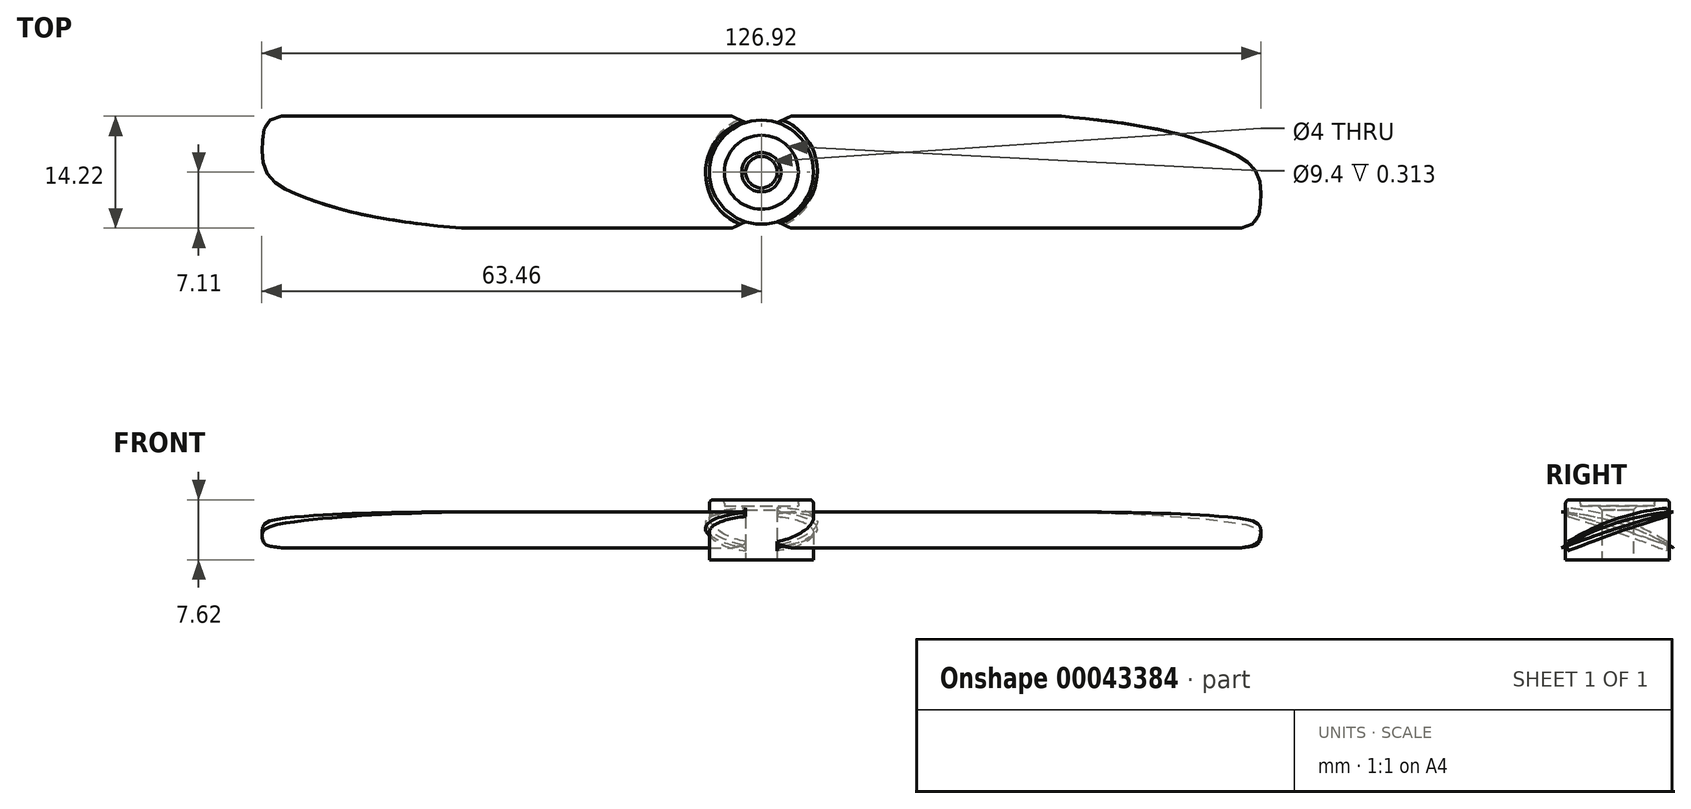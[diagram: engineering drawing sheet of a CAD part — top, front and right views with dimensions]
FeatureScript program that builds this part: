
annotation { "Feature Type Name" : "Feature", "Feature Type Description" : "" }
export const myFeature = defineFeature(function(context is Context, id is Id, definition is map)
    precondition{}
    {
        {
            var Q0;
            Q0=qCreatedBy(makeId("Front.planeOp"),FACE);
            var sketch = newSketch(context, id + "F0", { "sketchPlane" : qUnion([Q0])});
            skLineSegment(sketch, "E0", {"start": v(0, 0) * mm, "end": v(0, 9.6) * mm, "construction": true});
            skLineSegment(sketch, "E1", {"start": v(2, 0) * mm, "end": v(2, 6.8) * mm});
            skLineSegment(sketch, "E2", {"start": v(2, 6.8) * mm, "end": v(4.7, 6.8) * mm});
            skLineSegment(sketch, "E3", {"start": v(4.7, 6.8) * mm, "end": v(4.7, 7.62) * mm});
            skLineSegment(sketch, "E4", {"start": v(4.7, 7.62) * mm, "end": v(6.6, 7.62) * mm});
            skLineSegment(sketch, "E5", {"start": v(6.6, 7.62) * mm, "end": v(6.6, 0) * mm});
            skLineSegment(sketch, "E6", {"start": v(6.6, 0) * mm, "end": v(2, 0) * mm});
            skSolve(sketch);
        }
        {
            var Q0;
            Q0 = qSketchRegion(id + "F0", true);
            var Q1;
            Q1=sQuery(id+"F0.wireOp",EDGE,"E0");
            revolve(context, id + "F1", {"entities" : qUnion([Q0]), "axis" : qUnion([Q1]), "revolveType" : RevolveType.FULL});
        }
        {
            var Q0;
            Q0=makeQuery(id+"F1.opRevolve","SWEPT_EDGE",EDGE,{"disambiguationData":[OSD([sQuery(id+"F0.wireOp",EDGE,"E1"),sQuery(id+"F0.wireOp",EDGE,"E2")])]});
            chamfer(context, id + "F2", {"entities" : qUnion([Q0]), "width" : .5 * mm, "tangentPropagation" : true});
        }
        {
            var Q0;
            Q0=makeQuery(id+"F1.opRevolve","SWEPT_EDGE",EDGE,{"disambiguationData":[OSD([sQuery(id+"F0.wireOp",EDGE,"E4"),sQuery(id+"F0.wireOp",EDGE,"E5")])]});
            var Q1;
            Q1=makeQuery(id+"F1.opRevolve","SWEPT_EDGE",EDGE,{"disambiguationData":[OSD([sQuery(id+"F0.wireOp",EDGE,"E3"),sQuery(id+"F0.wireOp",EDGE,"E4")])]});
            fillet(context, id + "F3", {"entities" : qUnion([Q0, Q1]), "radius" : .5 * mm, "tangentPropagation" : true, "allowEdgeOverflow" : false});
        }
        {
            var Q0;
            Q0=qCreatedBy(makeId("Right.planeOp"),FACE);
            cPlane(context, id + "F4", {"entities" : qUnion([Q0]), "cplaneType" : CPlaneType.OFFSET, "offset" : 2 * mm, "width" : 152.4 * mm, "height" : 152.4 * mm});
        }
        {
            var Q0;
            Q0=qCreatedBy(id+"F4.planeOp",FACE);
            var sketch = newSketch(context, id + "F5", { "sketchPlane" : qUnion([Q0])});
            skFitSpline(sketch, "E7", {"points": [v(7.11, 6.1) * mm, v(-7.11, 1.52) * mm], "startDerivative": vector(-15.31, -1.42) * mm, "endDerivative": vector(-14.1, -8.25) * mm});
            skFitSpline(sketch, "E8", {"points": [v(7.11, 6.1) * mm, v(-7.11, 1.52) * mm], "startDerivative": vector(-15.85, -4.38) * mm, "endDerivative": vector(-15.17, -5.64) * mm});
            skSolve(sketch);
        }
        {
            var Q0;
            Q0 = qSketchRegion(id + "F5", true);
            extrude(context, id + "F6", {"entities" : qUnion([Q0]), "depth" : 61.47 * mm});
        }
        {
            var Q0;
            Q0=qCreatedBy(makeId("Top.planeOp"),FACE);
            var sketch = newSketch(context, id + "F7", { "sketchPlane" : qUnion([Q0])});
            skLineSegment(sketch, "E9", {"start": v(2, 6.3) * mm, "end": v(4.8, 7.6) * mm});
            skLineSegment(sketch, "E10", {"start": v(4.8, 7.6) * mm, "end": v(31.75, 7.6) * mm});
            skFitSpline(sketch, "E11", {"points": [v(31.75, 7.6) * mm, v(58.38, 3.04) * mm, v(62.88, 0) * mm, v(63.3, -4.8) * mm, v(52.06, -7.52) * mm], "startDerivative": vector(127.56, -8.25) * mm, "endDerivative": vector(-120.05, 0.74) * mm});
            skLineSegment(sketch, "E12", {"start": v(52.06, -7.52) * mm, "end": v(4.63, -7.52) * mm});
            skLineSegment(sketch, "E13", {"start": v(4.63, -7.52) * mm, "end": v(2, -6.3) * mm});
            skLineSegment(sketch, "E14", {"start": v(2, -6.3) * mm, "end": v(0.7, -9.1) * mm});
            skLineSegment(sketch, "E15", {"start": v(0.7, -9.1) * mm, "end": v(68.4, -9.1) * mm});
            skLineSegment(sketch, "E16", {"start": v(68.4, -9.1) * mm, "end": v(68.4, 10.53) * mm});
            skLineSegment(sketch, "E17", {"start": v(68.4, 10.53) * mm, "end": v(0.95, 10.53) * mm});
            skLineSegment(sketch, "E18", {"start": v(0.95, 10.53) * mm, "end": v(2, 6.3) * mm});
            skSolve(sketch);
        }
        {
            var Q0;
            Q0 = qSketchRegion(id + "F7", true);
            extrude(context, id + "F8", {"entities" : qUnion([Q0]), "operationType" : NewBodyOperationType.REMOVE, "endBound" : BoundingType.THROUGH_ALL, "depth" : 25.4 * mm});
        }
        {
            var Q0;
            Q0=makeQuery(id+"F6.opExtrude","SWEPT_BODY",BODY,{"disambiguationData":[OSD([sQuery(id+"F5.wireOp",EDGE,"E7"),sQuery(id+"F5.wireOp",EDGE,"E8")])]});
            var Q1;
            Q1=sQuery(id+"F0.wireOp",EDGE,"E0");
            circularPattern(context, id + "F9", {"entities" : qUnion([Q0]), "axis" : qUnion([Q1]), "angle" : 180 * degree, "instanceCount" : 2});
        }
        {
            var Q0;
            Q0=makeQuery(id+"F1.opRevolve","SWEPT_BODY",BODY,{"disambiguationData":[OSD([sQuery(id+"F0.wireOp",EDGE,"E1"),sQuery(id+"F0.wireOp",EDGE,"E2"),sQuery(id+"F0.wireOp",EDGE,"E3"),sQuery(id+"F0.wireOp",EDGE,"E4"),sQuery(id+"F0.wireOp",EDGE,"E5"),sQuery(id+"F0.wireOp",EDGE,"E6")])]});
            var Q1;
            Q1=makeQuery(id+"F6.opExtrude","SWEPT_BODY",BODY,{"disambiguationData":[OSD([sQuery(id+"F5.wireOp",EDGE,"E7"),sQuery(id+"F5.wireOp",EDGE,"E8")])]});
            var Q2;
            Q2=makeQuery(id+"F9.opPattern","COPY",BODY,{"derivedFrom":makeQuery(id+"F6.opExtrude","SWEPT_BODY",BODY,{"disambiguationData":[OSD([sQuery(id+"F5.wireOp",EDGE,"E7"),sQuery(id+"F5.wireOp",EDGE,"E8")])]}),"instanceName":"1"});
            booleanBodies(context, id + "F10", {"operationType" : BooleanOperationType.UNION, "tools" : qUnion([Q0, Q1, Q2])});
        }
        {
            var Q0;
            Q0=makeQuery(id+"F10.opBoolean","INTERSECT",EDGE,{"derivedFrom":[makeQuery(id+"F1.opRevolve","SWEPT_FACE",FACE,{"disambiguationData":[OSD([sQuery(id+"F0.wireOp",EDGE,"E5")])]}),makeQuery(id+"F6.opExtrude","SWEPT_FACE",FACE,{"disambiguationData":[OSD([sQuery(id+"F5.wireOp",EDGE,"E7")])]})]});
            var Q1;
            Q1=makeQuery(id+"F10.opBoolean","INTERSECT",EDGE,{"derivedFrom":[makeQuery(id+"F1.opRevolve","SWEPT_FACE",FACE,{"disambiguationData":[OSD([sQuery(id+"F0.wireOp",EDGE,"E5")])]}),makeQuery(id+"F6.opExtrude","SWEPT_FACE",FACE,{"disambiguationData":[OSD([sQuery(id+"F5.wireOp",EDGE,"E8")])]})]});
            var Q2;
            Q2=makeQuery(id+"F10.opBoolean","INTERSECT",EDGE,{"derivedFrom":[makeQuery(id+"F1.opRevolve","SWEPT_FACE",FACE,{"disambiguationData":[OSD([sQuery(id+"F0.wireOp",EDGE,"E5")])]}),makeQuery(id+"F9.opPattern","COPY",FACE,{"derivedFrom":makeQuery(id+"F6.opExtrude","SWEPT_FACE",FACE,{"disambiguationData":[OSD([sQuery(id+"F5.wireOp",EDGE,"E7")])]}),"instanceName":"1"})]});
            var Q3;
            Q3=makeQuery(id+"F10.opBoolean","INTERSECT",EDGE,{"derivedFrom":[makeQuery(id+"F1.opRevolve","SWEPT_FACE",FACE,{"disambiguationData":[OSD([sQuery(id+"F0.wireOp",EDGE,"E5")])]}),makeQuery(id+"F9.opPattern","COPY",FACE,{"derivedFrom":makeQuery(id+"F6.opExtrude","SWEPT_FACE",FACE,{"disambiguationData":[OSD([sQuery(id+"F5.wireOp",EDGE,"E8")])]}),"instanceName":"1"})]});
            fillet(context, id + "F11", {"entities" : qUnion([Q0, Q1, Q2, Q3]), "radius" : .5 * mm, "tangentPropagation" : true, "allowEdgeOverflow" : false});
        }
    });
